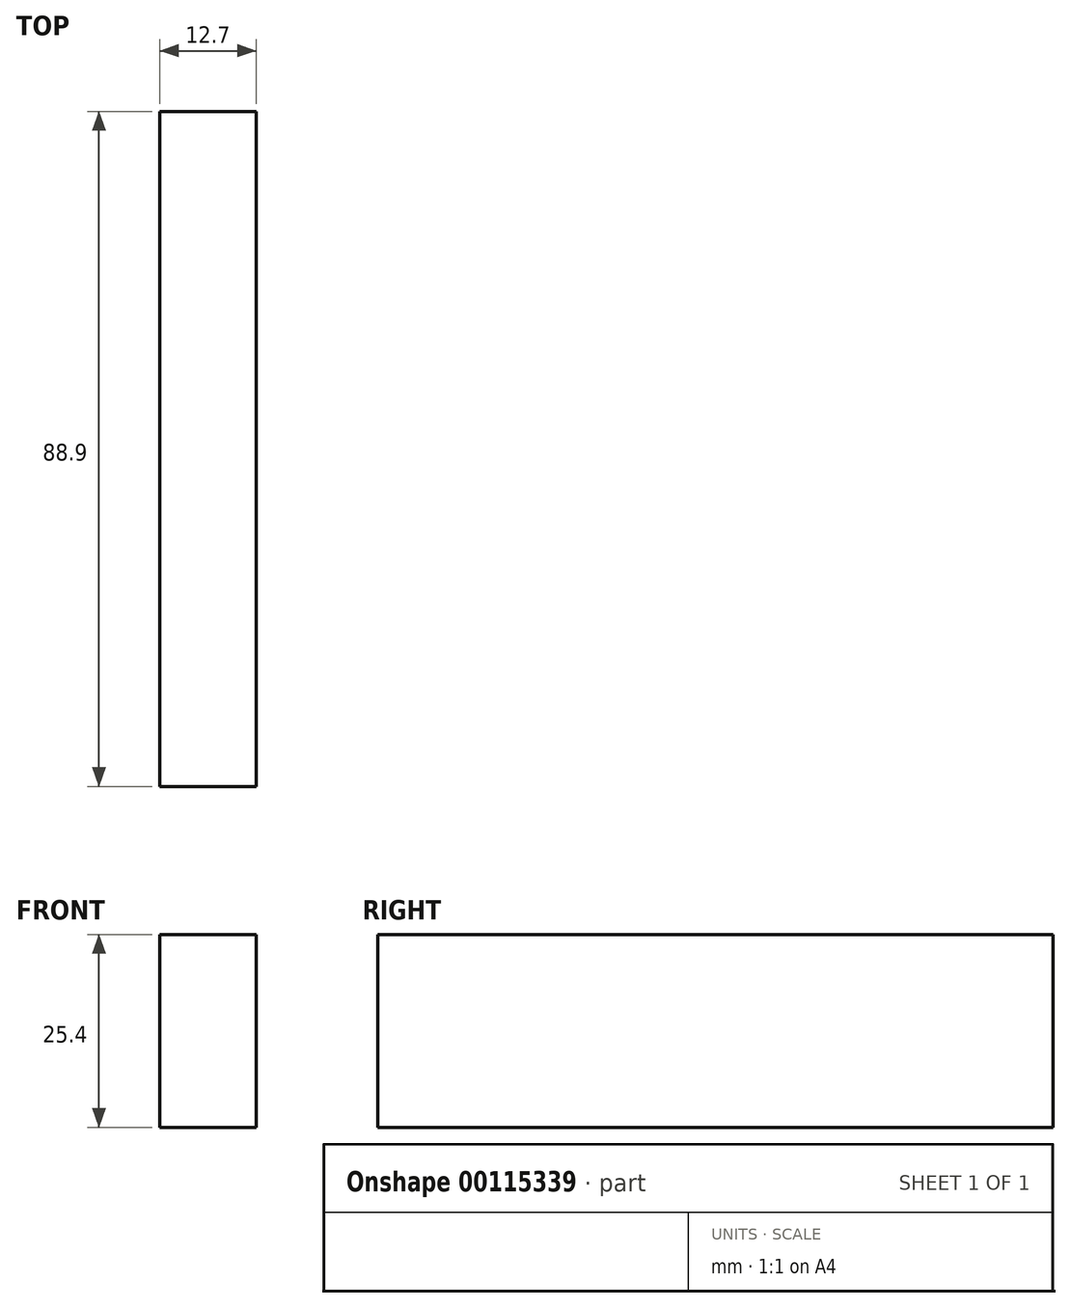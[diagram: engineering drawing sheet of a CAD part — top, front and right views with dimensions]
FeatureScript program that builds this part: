
annotation { "Feature Type Name" : "Feature", "Feature Type Description" : "" }
export const myFeature = defineFeature(function(context is Context, id is Id, definition is map)
    precondition{}
    {
        {
            var Q0;
            Q0=qCreatedBy(makeId("Top.planeOp"),FACE);
            var sketch = newSketch(context, id + "F0", { "sketchPlane" : qUnion([Q0])});
            skLineSegment(sketch, "E0.bottom", {"start": v(-12.7, 88.9) * mm, "end": v(0, 88.9) * mm});
            skLineSegment(sketch, "E0.top", {"start": v(-12.7, 0) * mm, "end": v(0, 0) * mm});
            skLineSegment(sketch, "E0.left", {"start": v(-12.7, 88.9) * mm, "end": v(-12.7, 0) * mm});
            skLineSegment(sketch, "E0.right", {"start": v(0, 88.9) * mm, "end": v(0, 0) * mm});
            skSolve(sketch);
        }
        {
            var Q0;
            Q0 = qSketchRegion(id + "F0", true);
            extrude(context, id + "F1", {"entities" : qUnion([Q0]), "depth" : 25.4 * mm});
        }
    });
